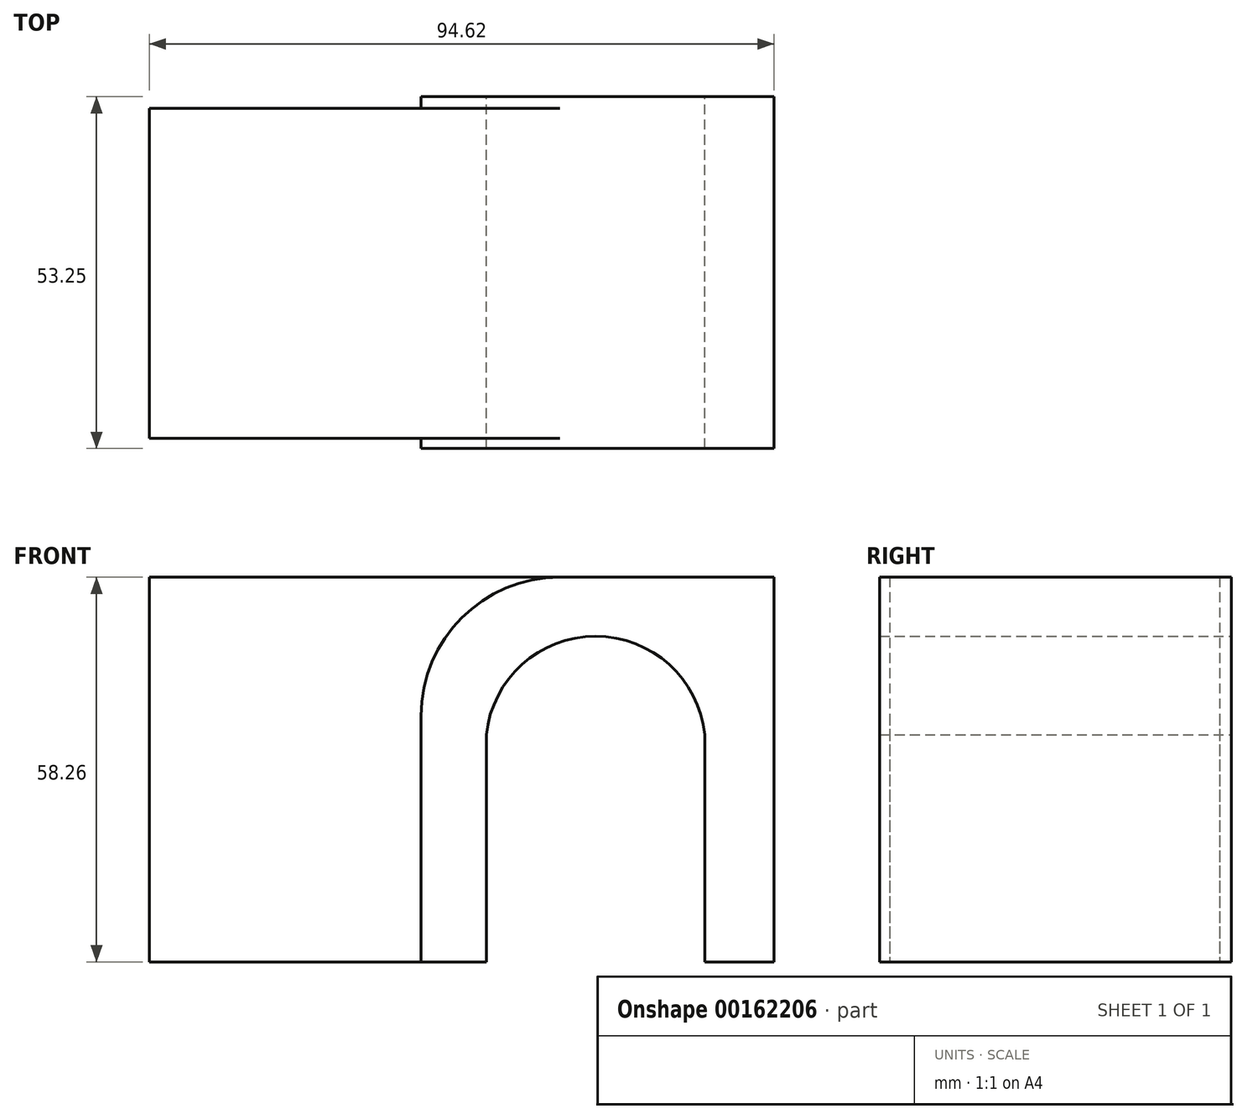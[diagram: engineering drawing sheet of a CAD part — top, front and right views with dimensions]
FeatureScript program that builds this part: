
annotation { "Feature Type Name" : "Feature", "Feature Type Description" : "" }
export const myFeature = defineFeature(function(context is Context, id is Id, definition is map)
    precondition{}
    {
        {
            var Q0;
            Q0=qCreatedBy(makeId("Front.planeOp"),FACE);
            var sketch = newSketch(context, id + "F0", { "sketchPlane" : qUnion([Q0])});
            skLineSegment(sketch, "E0.bottom", {"start": v(-47.31, 29.13) * mm, "end": v(47.31, 29.13) * mm});
            skLineSegment(sketch, "E0.top", {"start": v(-47.31, -29.13) * mm, "end": v(47.31, -29.13) * mm});
            skLineSegment(sketch, "E0.left", {"start": v(-47.31, 29.13) * mm, "end": v(-47.31, -29.13) * mm});
            skLineSegment(sketch, "E0.right", {"start": v(47.31, 29.13) * mm, "end": v(47.31, -29.13) * mm});
            skPoint(sketch, "E0.middle", {"position": v(0, 0) * mm});
            skLineSegment(sketch, "E1", {"start": v(36.83, -29.13) * mm, "end": v(36.83, 5.28) * mm});
            skLineSegment(sketch, "E2", {"start": v(3.74, -29.13) * mm, "end": v(3.74, 5.28) * mm});
            skArc(sketch, "E3", {"start": v(36.83, 5.28) * mm, "mid": v(20.28, 20.18) * mm, "end": v(3.74, 5.28) * mm});
            skLineSegment(sketch, "E4", {"start": v(-6.14, 29.13) * mm, "end": v(-6.14, -29.13) * mm});
            skSolve(sketch);
        }
        {
            var Q0;
            {var subQ0=sQuery(id+"F0.wireOp",EDGE,"E0.left");Q0=makeQuery(id+"F0.imprint","IMPRINT",FACE,{"disambiguationData":[TD([[makeQuery(id+"F0.imprint","IMPRINT",EDGE,{"derivedFrom":subQ0}),1.0]])]});}
            extrude(context, id + "F1", {"entities" : qUnion([Q0]), "depth" : 25 * mm, "hasSecondDirection" : true, "secondDirectionOppositeDirection" : true, "secondDirectionDepth" : 25 * mm});
        }
        {
            var Q0;
            {var subQ0=sQuery(id+"F0.wireOp",EDGE,"E0.right");Q0=makeQuery(id+"F0.imprint","IMPRINT",FACE,{"disambiguationData":[TD([[makeQuery(id+"F0.imprint","IMPRINT",EDGE,{"derivedFrom":subQ0}),-1.0]])]});}
            extrude(context, id + "F2", {"entities" : qUnion([Q0]), "operationType" : NewBodyOperationType.ADD, "depth" : 26.5 * mm, "hasSecondDirection" : true, "secondDirectionOppositeDirection" : true, "secondDirectionDepth" : 26.75 * mm});
        }
        {
            var Q0;
            {var subQ0=sQuery(id+"F0.wireOp",EDGE,"E4");var subQ1=sQuery(id+"F0.wireOp",EDGE,"E0.top");var subQ2=sQuery(id+"F0.wireOp",EDGE,"E0.bottom");Q0=makeQuery(id+"F2.boolean.opBoolean","SPLIT",EDGE,{"disambiguationData":[TD([makeQuery(id+"F1.opExtrude","CAP_FACE",FACE,{"disambiguationData":[OSD([subQ2,subQ1,sQuery(id+"F0.wireOp",EDGE,"E0.left"),subQ0])],"isStart":false})])],"derivedFrom":makeQuery(id+"F2.opExtrude","SWEPT_EDGE",EDGE,{"disambiguationData":[OSD([subQ2,subQ0])]})});}
            fillet(context, id + "F3", {"entities" : qUnion([Q0]), "radius" : 21 * mm, "tangentPropagation" : true, "allowEdgeOverflow" : false});
        }
        {
            var Q0;
            {var subQ0=sQuery(id+"F0.wireOp",EDGE,"E4");var subQ1=sQuery(id+"F0.wireOp",EDGE,"E0.top");var subQ2=sQuery(id+"F0.wireOp",EDGE,"E0.bottom");Q0=makeQuery(id+"F2.boolean.opBoolean","SPLIT",EDGE,{"disambiguationData":[TD([makeQuery(id+"F1.opExtrude","CAP_FACE",FACE,{"disambiguationData":[OSD([subQ2,subQ1,sQuery(id+"F0.wireOp",EDGE,"E0.left"),subQ0])],"isStart":true})])],"derivedFrom":makeQuery(id+"F2.opExtrude","SWEPT_EDGE",EDGE,{"disambiguationData":[OSD([subQ2,subQ0])]})});}
            fillet(context, id + "F4", {"entities" : qUnion([Q0]), "radius" : 21 * mm, "tangentPropagation" : true, "allowEdgeOverflow" : false});
        }
    });
